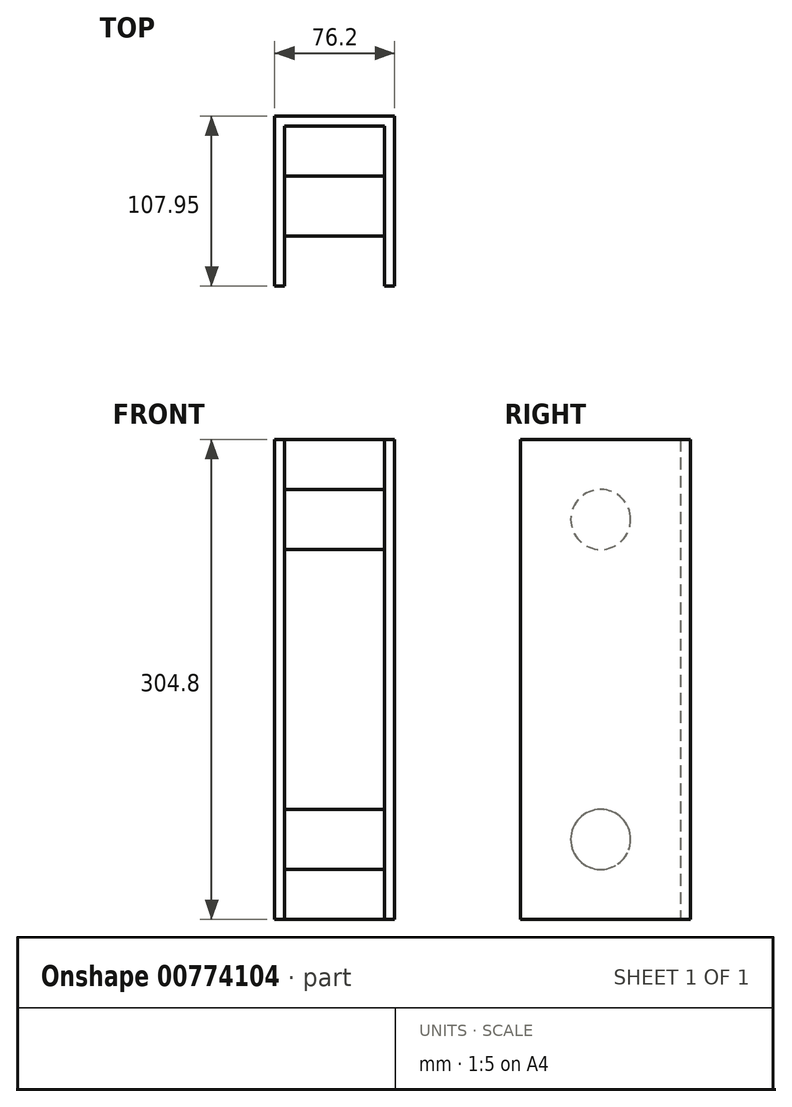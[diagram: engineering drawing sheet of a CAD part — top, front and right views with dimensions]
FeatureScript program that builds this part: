
annotation { "Feature Type Name" : "Feature", "Feature Type Description" : "" }
export const myFeature = defineFeature(function(context is Context, id is Id, definition is map)
    precondition{}
    {
        {
            var Q0;
            Q0=qCreatedBy(makeId("Top.planeOp"),FACE);
            var sketch = newSketch(context, id + "F0", { "sketchPlane" : qUnion([Q0])});
            skLineSegment(sketch, "E0.bottom", {"start": v(31.75, 50.8) * mm, "end": v(-31.75, 50.8) * mm});
            skLineSegment(sketch, "E0.left", {"start": v(31.75, 50.8) * mm, "end": v(31.75, -50.8) * mm});
            skLineSegment(sketch, "E0.right", {"start": v(-31.75, 50.8) * mm, "end": v(-31.75, -50.8) * mm});
            skPoint(sketch, "E0.middle", {"position": v(0, 0) * mm});
            skLineSegment(sketch, "E1.0", {"start": v(38.1, 57.15) * mm, "end": v(-38.1, 57.15) * mm});
            skLineSegment(sketch, "E2.0", {"start": v(38.1, 57.15) * mm, "end": v(38.1, -50.8) * mm});
            skLineSegment(sketch, "E3.0", {"start": v(-38.1, 57.15) * mm, "end": v(-38.1, -50.8) * mm});
            skLineSegment(sketch, "E4", {"start": v(-38.1, -50.8) * mm, "end": v(-31.75, -50.8) * mm});
            skLineSegment(sketch, "E5", {"start": v(31.75, -50.8) * mm, "end": v(38.1, -50.8) * mm});
            skSolve(sketch);
        }
        {
            var Q0;
            Q0=makeQuery(id+"F0.imprint","IMPRINT",FACE,{"disambiguationData":[TD([[makeQuery(id+"F0.imprint","IMPRINT",EDGE,{"derivedFrom":sQuery(id+"F0.wireOp",EDGE,"E0.bottom")}),-1.0]])]});
            extrude(context, id + "F1", {"entities" : qUnion([Q0]), "depth" : 152.4 * mm, "offsetDistance" : 25.4 * mm, "hasSecondDirection" : true, "secondDirectionOppositeDirection" : true, "secondDirectionDepth" : 152.4 * mm});
        }
        {
            var Q0;
            Q0=makeQuery(id+"F1.opExtrude","SWEPT_FACE",FACE,{"disambiguationData":[OSD([sQuery(id+"F0.wireOp",EDGE,"E3.0")])]});
            var sketch = newSketch(context, id + "F2", { "sketchPlane" : qUnion([Q0])});
            skCircle(sketch, "E6", {"center": v(0, 101.6) * mm, "radius": 19.05 * mm});
            skSolve(sketch);
        }
        {
            var Q0;
            Q0 = qSketchRegion(id + "F2", true);
            extrude(context, id + "F3", {"entities" : qUnion([Q0]), "operationType" : NewBodyOperationType.ADD, "oppositeDirection" : true, "depth" : 76.2 * mm, "offsetDistance" : 25.4 * mm});
        }
        {
            var Q0;
            Q0=makeQuery(id+"F1.opExtrude","SWEPT_BODY",BODY,{"disambiguationData":[OSD([sQuery(id+"F0.wireOp",EDGE,"E0.bottom"),sQuery(id+"F0.wireOp",EDGE,"E0.left"),sQuery(id+"F0.wireOp",EDGE,"E0.right"),sQuery(id+"F0.wireOp",EDGE,"E1.0"),sQuery(id+"F0.wireOp",EDGE,"E2.0"),sQuery(id+"F0.wireOp",EDGE,"E3.0"),sQuery(id+"F0.wireOp",EDGE,"E4"),sQuery(id+"F0.wireOp",EDGE,"E5")])]});
            var Q1;
            Q1=qCreatedBy(makeId("Top.planeOp"),FACE);
            mirror(context, id + "F4", {"operationType" : NewBodyOperationType.ADD, "entities" : qUnion([Q0]), "mirrorPlane" : qUnion([Q1])});
        }
    });
